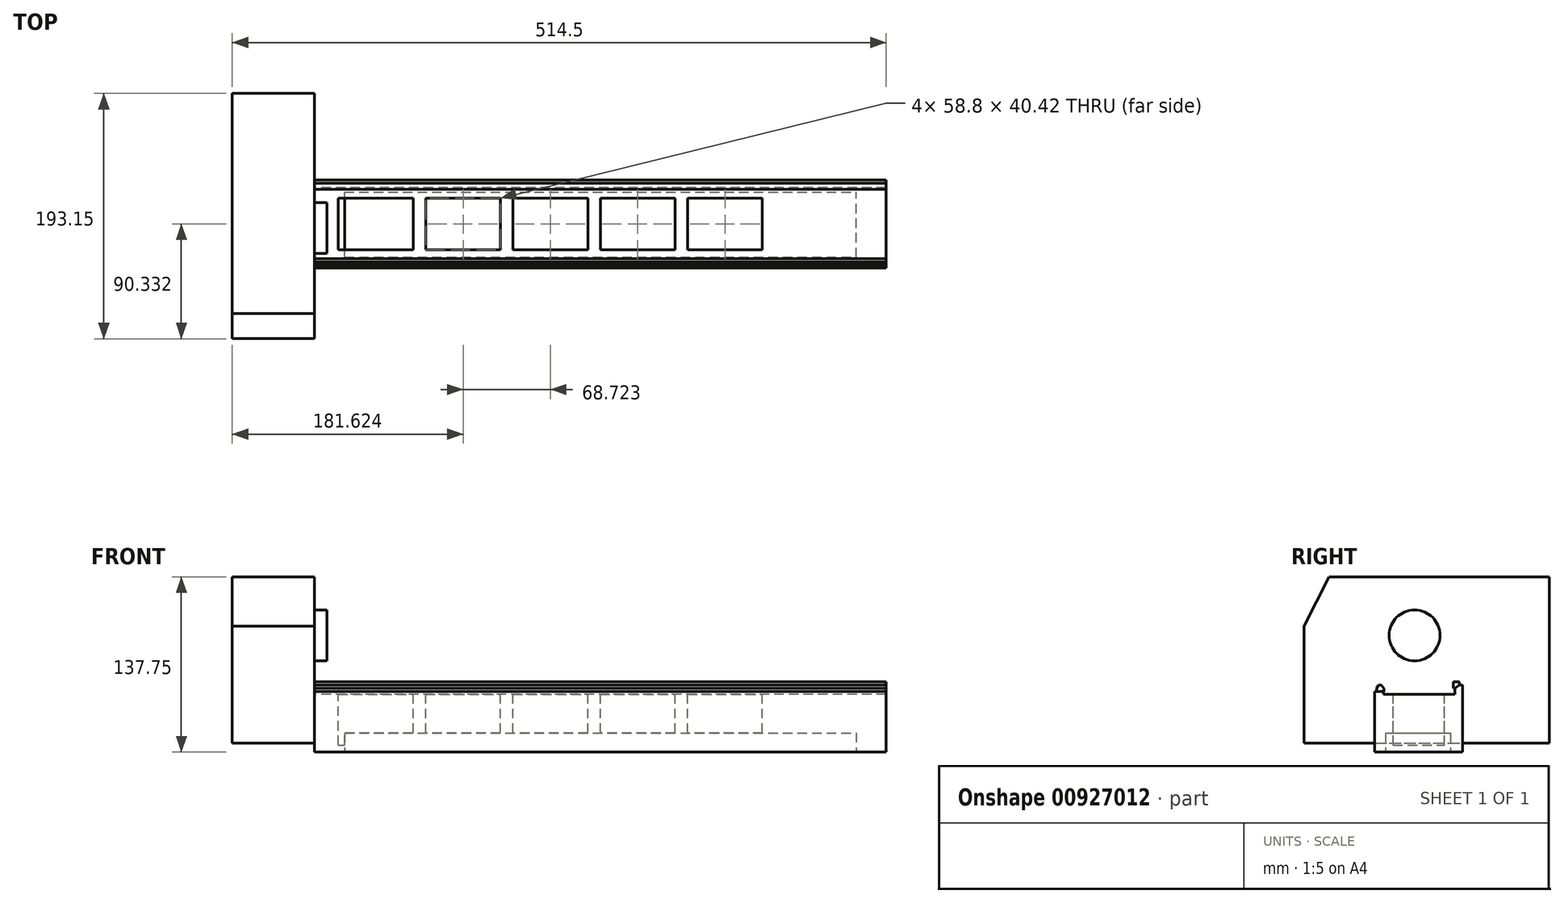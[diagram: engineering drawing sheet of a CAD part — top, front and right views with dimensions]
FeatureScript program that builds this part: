
annotation { "Feature Type Name" : "Feature", "Feature Type Description" : "" }
export const myFeature = defineFeature(function(context is Context, id is Id, definition is map)
    precondition{}
    {
        {
            var Q0;
            Q0=qCreatedBy(makeId("Right.planeOp"),FACE);
            var sketch = newSketch(context, id + "F0", { "sketchPlane" : qUnion([Q0])});
            skCircle(sketch, "E0", {"center": v(0, 16.75) * mm, "radius": 20 * mm});
            skLineSegment(sketch, "E1", {"start": v(-87.04, -68.2) * mm, "end": v(106.11, -68.2) * mm});
            skLineSegment(sketch, "E2", {"start": v(106.11, -68.2) * mm, "end": v(106.11, 62.75) * mm});
            skLineSegment(sketch, "E3", {"start": v(106.11, 62.75) * mm, "end": v(-67.34, 62.75) * mm});
            skLineSegment(sketch, "E4", {"start": v(-67.34, 62.75) * mm, "end": v(-87.04, 24) * mm});
            skLineSegment(sketch, "E5", {"start": v(-87.04, 24) * mm, "end": v(-87.04, -68.2) * mm});
            skLineSegment(sketch, "E6", {"start": v(-31.39, -75) * mm, "end": v(37.78, -75) * mm});
            skLineSegment(sketch, "E7", {"start": v(37.78, -75) * mm, "end": v(37.78, -22.25) * mm});
            skLineSegment(sketch, "E8", {"start": v(37.78, -22.25) * mm, "end": v(35.3, -22.25) * mm});
            skLineSegment(sketch, "E9", {"start": v(35.3, -22.25) * mm, "end": v(35.3, -19.92) * mm});
            skLineSegment(sketch, "E10", {"start": v(35.3, -19.92) * mm, "end": v(30.52, -19.92) * mm});
            skLineSegment(sketch, "E11", {"start": v(30.52, -19.92) * mm, "end": v(30.52, -24.9) * mm});
            skLineSegment(sketch, "E12", {"start": v(30.52, -24.9) * mm, "end": v(31.8, -24.9) * mm});
            skLineSegment(sketch, "E13", {"start": v(31.8, -24.9) * mm, "end": v(31.8, -29.56) * mm});
            skLineSegment(sketch, "E14", {"start": v(31.8, -29.56) * mm, "end": v(-24.6, -29.56) * mm});
            skLineSegment(sketch, "E15", {"start": v(-24.6, -29.56) * mm, "end": v(-24.6, -27.41) * mm});
            skLineSegment(sketch, "E16", {"start": v(-24.6, -27.41) * mm, "end": v(-24.02, -27.41) * mm});
            skLineSegment(sketch, "E17", {"start": v(-24.02, -27.41) * mm, "end": v(-24.02, -24.93) * mm});
            skLineSegment(sketch, "E18", {"start": v(-24.02, -24.93) * mm, "end": v(-26.48, -22.25) * mm});
            skLineSegment(sketch, "E19", {"start": v(-26.48, -22.25) * mm, "end": v(-28.28, -22.25) * mm});
            skLineSegment(sketch, "E20", {"start": v(-28.28, -22.25) * mm, "end": v(-29.8, -24.93) * mm});
            skLineSegment(sketch, "E21", {"start": v(-29.8, -24.93) * mm, "end": v(-29.8, -27.55) * mm});
            skLineSegment(sketch, "E22", {"start": v(-29.8, -27.55) * mm, "end": v(-31.39, -27.55) * mm});
            skLineSegment(sketch, "E23", {"start": v(-31.39, -27.55) * mm, "end": v(-31.39, -75) * mm});
            skLineSegment(sketch, "E24", {"start": v(35.3, -22.25) * mm, "end": v(31.8, -24.9) * mm});
            skLineSegment(sketch, "E25", {"start": v(-29.8, -27.55) * mm, "end": v(-24.6, -27.41) * mm});
            skSolve(sketch);
        }
        {
            var Q0;
            {var subQ6=sQuery(id+"F0.wireOp",EDGE,"okFbSqyt-2aSX-i3G5-wLgx-11pQmf4F1vWb");Q0=makeQuery(id+"F0.imprint","IMPRINT",FACE,{"disambiguationData":[TD([[makeQuery(id+"F0.imprint","IMPRINT",EDGE,{"derivedFrom":subQ6}),1.0]])]});}
            var Q1;
            Q1=makeQuery(id+"F0.imprint","IMPRINT",FACE,{"disambiguationData":[TD([[makeQuery(id+"F0.imprint","IMPRINT",EDGE,{"derivedFrom":sQuery(id+"F0.wireOp",EDGE,"E0")}),-1.0]])]});
            var Q2;
            Q2=makeQuery(id+"F0.imprint","IMPRINT",FACE,{"disambiguationData":[TD([[makeQuery(id+"F0.imprint","IMPRINT",EDGE,{"derivedFrom":sQuery(id+"F0.wireOp",EDGE,"E0")}),1.0]])]});
            var Q3;
            Q3=makeQuery(id+"F0.imprint","IMPRINT",FACE,{"disambiguationData":[TD([[makeQuery(id+"F0.imprint","IMPRINT",EDGE,{"derivedFrom":sQuery(id+"F0.wireOp",EDGE,"E1")}),1.0]])]});
            var Q4;
            Q4=makeQuery(id+"F0.imprint","IMPRINT",FACE,{"disambiguationData":[TD([[makeQuery(id+"F0.imprint","IMPRINT",EDGE,{"derivedFrom":sQuery(id+"F0.wireOp",EDGE,"f9dfe43e-a8dd-4006-a5e7-0a65c4802650")}),1.0]])]});
            var Q5;
            {var subQ0=sQuery(id+"F0.wireOp",EDGE,"E8");Q5=makeQuery(id+"F0.imprint","IMPRINT",FACE,{"disambiguationData":[TD([[makeQuery(id+"F0.imprint","IMPRINT",EDGE,{"derivedFrom":subQ0}),1.0]])]});}
            var Q6;
            Q6=makeQuery(id+"F0.imprint","IMPRINT",FACE,{"disambiguationData":[TD([[makeQuery(id+"F0.imprint","IMPRINT",EDGE,{"derivedFrom":sQuery(id+"F0.wireOp",EDGE,"E9")}),1.0]])]});
            var Q7;
            Q7=makeQuery(id+"F0.imprint","IMPRINT",FACE,{"disambiguationData":[TD([[makeQuery(id+"F0.imprint","IMPRINT",EDGE,{"derivedFrom":sQuery(id+"F0.wireOp",EDGE,"E16")}),1.0]])]});
            extrude(context, id + "F1", {"entities" : qUnion([Q0, Q1, Q2, Q3, Q4, Q5, Q6, Q7]), "oppositeDirection" : true, "depth" : 64.5 * mm, "offsetDistance" : 25 * mm});
        }
        {
            var Q0;
            {var subQ5=sQuery(id+"F0.wireOp",EDGE,"E6");Q0=makeQuery(id+"F0.imprint","IMPRINT",FACE,{"disambiguationData":[TD([[makeQuery(id+"F0.imprint","IMPRINT",EDGE,{"derivedFrom":subQ5}),1.0]])]});}
            var Q1;
            {var subQ0=sQuery(id+"F0.wireOp",EDGE,"E8");Q1=makeQuery(id+"F0.imprint","IMPRINT",FACE,{"disambiguationData":[TD([[makeQuery(id+"F0.imprint","IMPRINT",EDGE,{"derivedFrom":subQ0}),1.0]])]});}
            extrude(context, id + "F2", {"entities" : qUnion([Q0, Q1]), "depth" : 450 * mm, "offsetDistance" : 25 * mm});
        }
        {
            var Q0;
            Q0=makeQuery(id+"F2.opExtrude","SWEPT_FACE",FACE,{"disambiguationData":[OSD([sQuery(id+"F0.wireOp",EDGE,"E6")])]});
            var sketch = newSketch(context, id + "F3", { "sketchPlane" : qUnion([Q0])});
            skLineSegment(sketch, "E26.bottom", {"start": v(23.78, 22.8) * mm, "end": v(426.56, 22.8) * mm});
            skLineSegment(sketch, "E26.top", {"start": v(23.78, -28.28) * mm, "end": v(426.56, -28.28) * mm});
            skLineSegment(sketch, "E26.left", {"start": v(23.78, 22.8) * mm, "end": v(23.78, -28.28) * mm});
            skLineSegment(sketch, "E26.right", {"start": v(426.56, 22.8) * mm, "end": v(426.56, -28.28) * mm});
            skSolve(sketch);
        }
        {
            var Q0;
            Q0 = qSketchRegion(id + "F3", true);
            extrude(context, id + "F4", {"entities" : qUnion([Q0]), "operationType" : NewBodyOperationType.REMOVE, "oppositeDirection" : true, "depth" : 15 * mm, "offsetDistance" : 25 * mm});
        }
        {
            var Q0;
            Q0=makeQuery(id+"F2.opExtrude","SWEPT_FACE",FACE,{"disambiguationData":[OSD([sQuery(id+"F0.wireOp",EDGE,"E14")])]});
            var sketch = newSketch(context, id + "F5", { "sketchPlane" : qUnion([Q0])});
            skLineSegment(sketch, "E27.bottom", {"start": v(19, 23.5) * mm, "end": v(77.8, 23.5) * mm});
            skLineSegment(sketch, "E27.top", {"start": v(19, -16.92) * mm, "end": v(77.8, -16.92) * mm});
            skLineSegment(sketch, "E27.left", {"start": v(19, 23.5) * mm, "end": v(19, -16.92) * mm});
            skLineSegment(sketch, "E27.right", {"start": v(77.8, 23.5) * mm, "end": v(77.8, -16.92) * mm});
            skLineSegment(sketch, "E28.bottom", {"start": v(87.72, 23.5) * mm, "end": v(146.52, 23.5) * mm});
            skLineSegment(sketch, "E28.top", {"start": v(87.72, -16.92) * mm, "end": v(146.52, -16.92) * mm});
            skLineSegment(sketch, "E28.left", {"start": v(87.72, 23.5) * mm, "end": v(87.72, -16.92) * mm});
            skLineSegment(sketch, "E28.right", {"start": v(146.52, 23.5) * mm, "end": v(146.52, -16.92) * mm});
            skLineSegment(sketch, "E29.bottom", {"start": v(156.45, 23.5) * mm, "end": v(215.25, 23.5) * mm});
            skLineSegment(sketch, "E29.top", {"start": v(156.45, -16.92) * mm, "end": v(215.25, -16.92) * mm});
            skLineSegment(sketch, "E29.left", {"start": v(156.45, 23.5) * mm, "end": v(156.45, -16.92) * mm});
            skLineSegment(sketch, "E29.right", {"start": v(215.25, 23.5) * mm, "end": v(215.25, -16.92) * mm});
            skLineSegment(sketch, "E30.bottom", {"start": v(225.17, 23.5) * mm, "end": v(283.97, 23.5) * mm});
            skLineSegment(sketch, "E30.top", {"start": v(225.17, -16.92) * mm, "end": v(283.97, -16.92) * mm});
            skLineSegment(sketch, "E30.left", {"start": v(225.17, 23.5) * mm, "end": v(225.17, -16.92) * mm});
            skLineSegment(sketch, "E30.right", {"start": v(283.97, 23.5) * mm, "end": v(283.97, -16.92) * mm});
            skLineSegment(sketch, "E31.bottom", {"start": v(293.9, 23.5) * mm, "end": v(352.7, 23.5) * mm});
            skLineSegment(sketch, "E31.top", {"start": v(293.9, -16.92) * mm, "end": v(352.7, -16.92) * mm});
            skLineSegment(sketch, "E31.left", {"start": v(293.9, 23.5) * mm, "end": v(293.9, -16.92) * mm});
            skLineSegment(sketch, "E31.right", {"start": v(352.7, 23.5) * mm, "end": v(352.7, -16.92) * mm});
            skLineSegment(sketch, "E32", {"start": v(77.8, 23.5) * mm, "end": v(87.72, 23.5) * mm});
            skLineSegment(sketch, "E33", {"start": v(87.72, -16.92) * mm, "end": v(77.8, -16.92) * mm});
            skLineSegment(sketch, "E34", {"start": v(146.52, 23.5) * mm, "end": v(156.45, 23.5) * mm});
            skLineSegment(sketch, "E35", {"start": v(156.45, -16.92) * mm, "end": v(146.52, -16.92) * mm});
            skLineSegment(sketch, "E36", {"start": v(215.25, -16.92) * mm, "end": v(225.17, -16.92) * mm});
            skLineSegment(sketch, "E37", {"start": v(225.17, 23.5) * mm, "end": v(215.25, 23.5) * mm});
            skLineSegment(sketch, "E38", {"start": v(283.97, 23.5) * mm, "end": v(293.9, 23.5) * mm});
            skLineSegment(sketch, "E39", {"start": v(293.9, -16.92) * mm, "end": v(283.97, -16.92) * mm});
            skSolve(sketch);
        }
        {
            var Q0;
            Q0=makeQuery(id+"F5.imprint","IMPRINT",FACE,{"disambiguationData":[TD([[makeQuery(id+"F5.imprint","IMPRINT",EDGE,{"derivedFrom":sQuery(id+"F5.wireOp",EDGE,"E27.bottom")}),-1.0]])]});
            var Q1;
            Q1=makeQuery(id+"F5.imprint","IMPRINT",FACE,{"disambiguationData":[TD([[makeQuery(id+"F5.imprint","IMPRINT",EDGE,{"derivedFrom":sQuery(id+"F5.wireOp",EDGE,"E31.bottom")}),-1.0]])]});
            var Q2;
            Q2=makeQuery(id+"F5.imprint","IMPRINT",FACE,{"disambiguationData":[TD([[makeQuery(id+"F5.imprint","IMPRINT",EDGE,{"derivedFrom":sQuery(id+"F5.wireOp",EDGE,"E28.bottom")}),-1.0]])]});
            var Q3;
            Q3=makeQuery(id+"F5.imprint","IMPRINT",FACE,{"disambiguationData":[TD([[makeQuery(id+"F5.imprint","IMPRINT",EDGE,{"derivedFrom":sQuery(id+"F5.wireOp",EDGE,"E29.bottom")}),-1.0]])]});
            var Q4;
            Q4=makeQuery(id+"F5.imprint","IMPRINT",FACE,{"disambiguationData":[TD([[makeQuery(id+"F5.imprint","IMPRINT",EDGE,{"derivedFrom":sQuery(id+"F5.wireOp",EDGE,"E30.bottom")}),-1.0]])]});
            extrude(context, id + "F6", {"entities" : qUnion([Q0, Q1, Q2, Q3, Q4]), "operationType" : NewBodyOperationType.REMOVE, "oppositeDirection" : true, "depth" : 40 * mm, "offsetDistance" : 25 * mm});
        }
        {
            var Q0;
            Q0=makeQuery(id+"F0.imprint","IMPRINT",FACE,{"disambiguationData":[TD([[makeQuery(id+"F0.imprint","IMPRINT",EDGE,{"derivedFrom":sQuery(id+"F0.wireOp",EDGE,"E16")}),1.0]])]});
            var Q1;
            Q1=makeQuery(id+"F0.imprint","IMPRINT",FACE,{"disambiguationData":[TD([[makeQuery(id+"F0.imprint","IMPRINT",EDGE,{"derivedFrom":sQuery(id+"F0.wireOp",EDGE,"E9")}),1.0]])]});
            extrude(context, id + "F7", {"entities" : qUnion([Q0, Q1]), "depth" : 450 * mm, "offsetDistance" : 25 * mm});
        }
        {
            var Q0;
            Q0=makeQuery(id+"F0.imprint","IMPRINT",FACE,{"disambiguationData":[TD([[makeQuery(id+"F0.imprint","IMPRINT",EDGE,{"derivedFrom":sQuery(id+"F0.wireOp",EDGE,"E0")}),1.0]])]});
            extrude(context, id + "F8", {"entities" : qUnion([Q0]), "depth" : 10 * mm, "offsetDistance" : 25 * mm});
        }
    });
